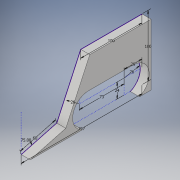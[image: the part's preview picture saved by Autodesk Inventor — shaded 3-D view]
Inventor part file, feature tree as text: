
AUTODESK INVENTOR PART (.ipt)
format: ipt  version: 2019 (Build 230136000, 136)  size: 115,200 bytes
history: native  units: mm
features: extrude x1, sketch x1
ambient origin geometry x8: Origin, YZ Plane, XZ Plane, XY Plane, X Axis, Y Axis, Z Axis, Center Point
bodies: Solid1 (feature_tree)
feature tree (2):
  extrude  "Extrusion1"  Depth=100.0mm
  sketch  "Sketch2"  dims[d10=100.0mm d11=100.0mm d12=197.0mm d13=60.0mm d14=75.0deg d15=24.0mm d16=29.0mm d17=73.0mm d18=26.0mm d19=26.0mm d20=15.0mm d21=0.0mm]
